# Revit family: Hager-Univers-IP55-D275-H2050-Cl.II-Steel_encl-PT-pt
name_source: partatom
category: Equipement électrique
units: mm (PartAtom-declared; Revit-internal decimal feet)

## family parameters
Configuration du panneau = Deux colonnes, circuits au sein
Cote de connecteur circulaire = Utiliser le diamètre
Couper avec des vides une fois chargée = Non
Hôte = Face
Partagée = Non
Point de calcul de pièce = Non
Type d'élément = Tableau de raccordement

## types (11) — shared parameters
Commentaires du type = Univers
EF000003 - Método de montagem = EV012274 - Instalação de piso
EF000007 - Cor = EV000270 - Cinzento
EF000040 - Altura = 2050 mm  [stored 6.72572 ft]
EF000049 - Profundidade = 275 mm  [stored 0.902231 ft]
EF000116 - Número RAL = 7035
EF000118 - Com tampa de montagem = Non
EF000266 - Número de linhas = 12
EF000339 - Tipo de difusor = EV004216 - Porta
EF001088 - Extensão possível = Oui
EF001131 - Profundidade interior = 275 mm  [stored 0.902231 ft]
EF001596 - Material do corpo = EV000179 - Aço
EF001613 - Integridade do circuito = EV000494 - Nenhum
EF002950 - Largura em número de módulos = 24
EF003532 - Adequado para uso no exterior = Non
EF004293 - Força de impacto = EV008784 - IK10
EF005474 - Grau de proteção (IP) = EV006420 - IP55
EF006306 - Com fecho = Non
EF007800 - Adequado para proteção contra raios = Non
EF008873 - Corrente nominal (In) = 800 A
EF009170 - Espessura do material do invólucro = 2 mm  [stored 0.00656168 ft]
EF009171 - Espessura do material da porta/tampa = 2 mm  [stored 0.00656168 ft]
EF009212 - Tipo de tampa = EV000116 - Fechado
EF015940 - Tampa com libertação de sobrepressão = Non
Fabricant = Hager
HG000002 - Com porta ou tampa = Oui
HG000003 - Gama = Univers
HG000006 - Encastrado = Non
HG000023 - Recinto de secção dupla = Non
HG000024 - Altura da secção inferior = 800 mm  [stored 2.62467 ft]
HG000026 - Instalação no chão = Oui
HG000027 - Altura da Plinta = 200 mm  [stored 0.656168 ft]
zero-valued in all types: EF000218 - Profundidade incorporada, Elévation par défaut

## per-type parameters (varying)
| type | EF000008 - Largura | EF000437 - Número de entradas de condutores | EF004427 - Número de módulos | EF004464 - Tipo de porta | EF006244 - Tampa/porta transparente | EF009554 - Número de aberturas para placas de flange | HG000004 - Referência do Fabricante | HG000009 - Porta dupla | HG000010 - Portas assimétricas |
| Instalação de piso IP55 L1050 A2050 P275  - FR24L2 | 1050 mm | 8 | 576 | EV003602 - Duplo | Oui | 8 | FR24L2 | Oui | Oui |
| Instalação de piso IP55 L1050 A2050 P275  - FR24S2 | 1050 mm | 8 | 576 | EV003602 - Duplo | Non | 8 | FR24S2 | Oui | Oui |
| Instalação de piso IP55 L1300 A2050 P275  - FR25L2 | 1300 mm  [stored 4.26509 ft] | 10 | 720 | EV003602 - Duplo | Oui | 10 | FR25L2 | Oui | Oui |
| Instalação de piso IP55 L1300 A2050 P275  - FR25S2 | 1300 mm  [stored 4.26509 ft] | 10 | 720 | EV003602 - Duplo | Non | 10 | FR25S2 | Oui | Oui |
| Instalação de piso IP55 L1550 A2050 P275  - FR26L2 | 1550 mm  [stored 5.0853 ft] | 12 | 864 | EV003602 - Duplo | Oui | 12 | FR26L2 | Oui | Oui |
| Instalação de piso IP55 L1550 A2050 P275  - FR26S2 | 1550 mm  [stored 5.0853 ft] | 12 | 864 | EV003602 - Duplo | Non | 12 | FR26S2 | Oui | Oui |
| Instalação de piso IP55 L300 A2050 P275  - FR21S2 | 300 mm | 2 | 144 | EV002646 - Único | Non | 2 | FR21S2 | Non | Non |
| Instalação de piso IP55 L550 A2050 P275  - FR22L2 | 550 mm | 4 | 288 | EV002646 - Único | Oui | 4 | FR22L2 | Non | Non |
| Instalação de piso IP55 L550 A2050 P275  - FR22S2 | 550 mm | 4 | 288 | EV002646 - Único | Non | 4 | FR22S2 | Non | Non |
| Instalação de piso IP55 L800 A2050 P275  - FR23L2 | 800 mm  [stored 2.62467 ft] | 6 | 432 | EV002646 - Único | Oui | 6 | FR23L2 | Non | Non |
| Instalação de piso IP55 L800 A2050 P275  - FR23S2 | 800 mm  [stored 2.62467 ft] | 6 | 432 | EV002646 - Único | Non | 6 | FR23S2 | Non | Non |

note: [stored X ft] marks values corroborated as IEEE doubles in the binary element streams (Revit-internal decimal feet)

## geometry (parser evidence)
native form markers: Sweep x10
no freeform markers — native parametric forms only
